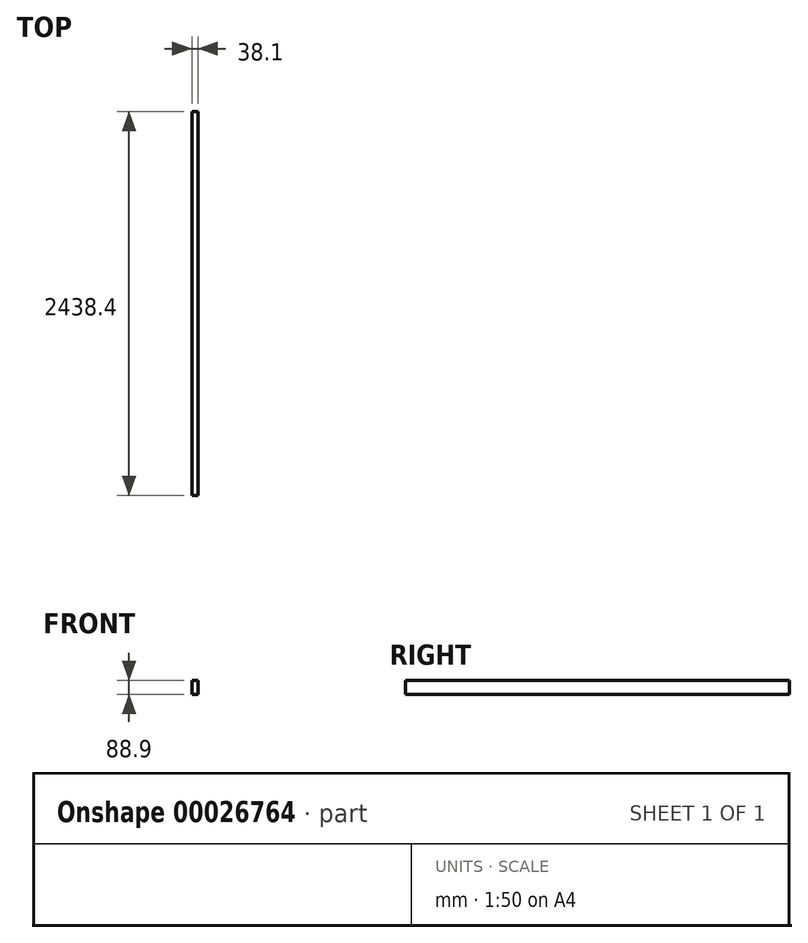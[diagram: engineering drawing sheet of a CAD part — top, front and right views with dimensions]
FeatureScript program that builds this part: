
annotation { "Feature Type Name" : "Feature", "Feature Type Description" : "" }
export const myFeature = defineFeature(function(context is Context, id is Id, definition is map)
    precondition{}
    {
        {
            var Q0;
            Q0=qCreatedBy(makeId("Front.planeOp"),FACE);
            var sketch = newSketch(context, id + "F0", { "sketchPlane" : qUnion([Q0])});
            skLineSegment(sketch, "E0.rect.bottom", {"start": v(-19.05, 44.45) * mm, "end": v(19.05, 44.45) * mm});
            skLineSegment(sketch, "E0.rect.top", {"start": v(-19.05, -44.45) * mm, "end": v(19.05, -44.45) * mm});
            skLineSegment(sketch, "E0.rect.left", {"start": v(-19.05, 44.45) * mm, "end": v(-19.05, -44.45) * mm});
            skLineSegment(sketch, "E0.rect.right", {"start": v(19.05, 44.45) * mm, "end": v(19.05, -44.45) * mm});
            skPoint(sketch, "E0.rect.middle", {"position": v(0, 0) * mm});
            skSolve(sketch);
        }
        {
            var Q0;
            Q0 = qSketchRegion(id + "F0", true);
            extrude(context, id + "F1", {"entities" : qUnion([Q0]), "depth" : 2438.4 * mm});
        }
    });
